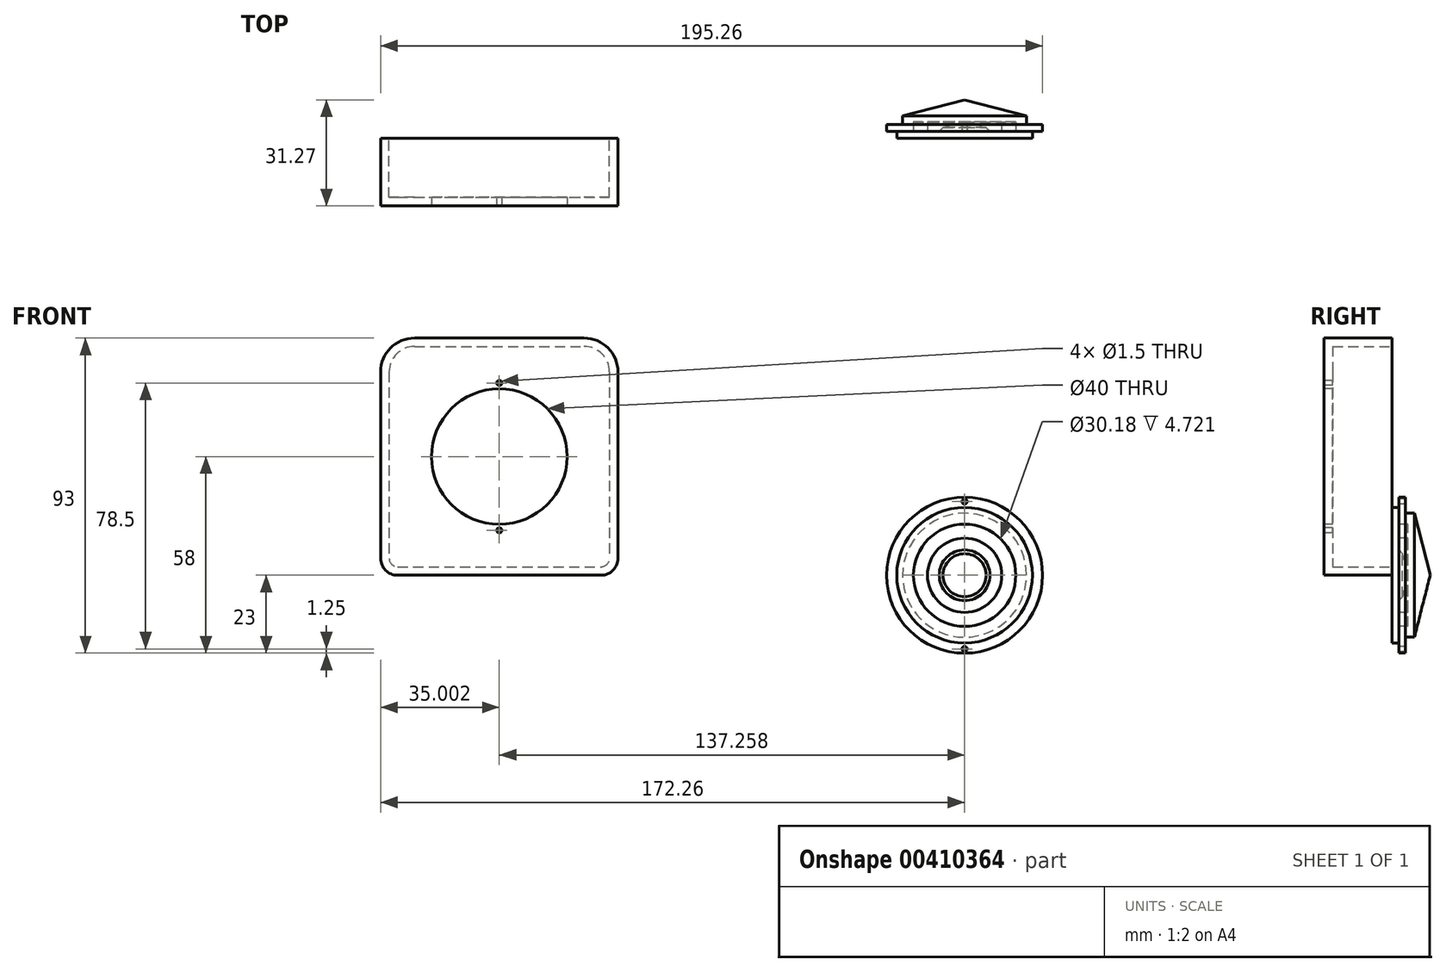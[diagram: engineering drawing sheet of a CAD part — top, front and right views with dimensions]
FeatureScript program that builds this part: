
annotation { "Feature Type Name" : "Feature", "Feature Type Description" : "" }
export const myFeature = defineFeature(function(context is Context, id is Id, definition is map)
    precondition{}
    {
        {
            var Q0;
            Q0=qCreatedBy(makeId("Right.planeOp"),FACE);
            var sketch = newSketch(context, id + "F0", { "sketchPlane" : qUnion([Q0])});
            skLineSegment(sketch, "E0", {"start": v(0, 20) * mm, "end": v(2, 20) * mm});
            skLineSegment(sketch, "E1", {"start": v(0, 20) * mm, "end": v(0, 15.09) * mm});
            skLineSegment(sketch, "E2", {"start": v(0, 15.09) * mm, "end": v(2, 15.09) * mm});
            skLineSegment(sketch, "E3", {"start": v(2, 11.08) * mm, "end": v(2.03, 10.95) * mm});
            skPoint(sketch, "E3.endSnap0", {"position": v(2.86, 0) * mm});
            skLineSegment(sketch, "E4", {"start": v(4.58, 0) * mm, "end": v(6.88, 0) * mm});
            skLineSegment(sketch, "E5", {"start": v(2, 20) * mm, "end": v(2, 23) * mm});
            skLineSegment(sketch, "E6", {"start": v(2, 23) * mm, "end": v(4, 23) * mm});
            skLineSegment(sketch, "E7", {"start": v(4, 23) * mm, "end": v(4, 19.74) * mm});
            skLineSegment(sketch, "E8", {"start": v(4, 19.74) * mm, "end": v(4, 18.29) * mm});
            skLineSegment(sketch, "E9", {"start": v(4, 18.29) * mm, "end": v(6.62, 18.29) * mm});
            skLineSegment(sketch, "E10", {"start": v(11.27, 0) * mm, "end": v(6.88, 0) * mm});
            skLineSegment(sketch, "E11", {"start": v(6.62, 18.29) * mm, "end": v(11.27, 0) * mm});
            skLineSegment(sketch, "E12", {"start": v(2, 15.09) * mm, "end": v(4.72, 15.09) * mm});
            skLineSegment(sketch, "E13", {"start": v(4.72, 15.09) * mm, "end": v(4.72, 10.95) * mm});
            skLineSegment(sketch, "E14", {"start": v(4.72, 10.95) * mm, "end": v(2.03, 10.95) * mm});
            skLineSegment(sketch, "E15", {"start": v(2.03, 10.95) * mm, "end": v(2.03, 7.48) * mm});
            skLineSegment(sketch, "E16", {"start": v(2.03, 7.48) * mm, "end": v(3.1, 6.34) * mm});
            skLineSegment(sketch, "E17.trimOffspring", {"start": v(3.1, 6.34) * mm, "end": v(4.58, 0) * mm});
            skSolve(sketch);
        }
        {
            var Q0;
            Q0 = qSketchRegion(id + "F0", true);
            var Q1;
            Q1=sQuery(id+"F0.wireOp",EDGE,"E4");
            revolve(context, id + "F1", {"entities" : qUnion([Q0]), "axis" : qUnion([Q1]), "revolveType" : RevolveType.FULL});
        }
        {
            var Q0;
            Q0=makeQuery(id+"F1.opRevolve","SWEPT_FACE",FACE,{"disambiguationData":[OSD([sQuery(id+"F0.wireOp",EDGE,"E5")])]});
            var sketch = newSketch(context, id + "F2", { "sketchPlane" : qUnion([Q0])});
            skCircle(sketch, "E18", {"center": v(0, 21.75) * mm, "radius": 0.75 * mm});
            skCircle(sketch, "E19.MirrorC", {"center": v(0, -21.75) * mm, "radius": 0.75 * mm});
            skSolve(sketch);
        }
        {
            var Q0;
            Q0 = qSketchRegion(id + "F2", true);
            extrude(context, id + "F3", {"entities" : qUnion([Q0]), "operationType" : NewBodyOperationType.REMOVE, "oppositeDirection" : true, "depth" : 25 * mm});
        }
        {
            var Q0;
            Q0=qCreatedBy(makeId("Front.planeOp"),FACE);
            var sketch = newSketch(context, id + "F4", { "sketchPlane" : qUnion([Q0])});
            skLineSegment(sketch, "E20.bottom", {"start": v(-162.26, 70) * mm, "end": v(-112.26, 70) * mm});
            skLineSegment(sketch, "E20.top", {"start": v(-167.26, 0) * mm, "end": v(-107.26, 0) * mm});
            skLineSegment(sketch, "E20.left", {"start": v(-172.26, 60) * mm, "end": v(-172.26, 5) * mm});
            skLineSegment(sketch, "E20.right", {"start": v(-102.26, 60) * mm, "end": v(-102.26, 5) * mm});
            skPoint(sketch, "E21.visualSharp", {"position": v(-172.26, 70) * mm});
            skArc(sketch, "E21.filletArc", {"start": v(-162.26, 70) * mm, "mid": v(-169.33, 67.07) * mm, "end": v(-172.26, 60) * mm});
            skPoint(sketch, "E22.visualSharp", {"position": v(-102.26, 70) * mm});
            skArc(sketch, "E22.filletArc", {"start": v(-102.26, 60) * mm, "mid": v(-105.19, 67.07) * mm, "end": v(-112.26, 70) * mm});
            skPoint(sketch, "E23.visualSharp", {"position": v(-172.26, 0) * mm});
            skArc(sketch, "E23.filletArc", {"start": v(-172.26, 5) * mm, "mid": v(-170.8, 1.46) * mm, "end": v(-167.26, 0) * mm});
            skPoint(sketch, "E24.visualSharp", {"position": v(-102.26, 0) * mm});
            skArc(sketch, "E24.filletArc", {"start": v(-107.26, 0) * mm, "mid": v(-103.72, 1.46) * mm, "end": v(-102.26, 5) * mm});
            skSolve(sketch);
        }
        {
            var Q0;
            Q0=makeQuery(id+"F4.imprint","IMPRINT",FACE,{"disambiguationData":[TD([[makeQuery(id+"F4.imprint","IMPRINT",EDGE,{"derivedFrom":sQuery(id+"F4.wireOp",EDGE,"E20.bottom")}),-1.0]])]});
            extrude(context, id + "F5", {"entities" : qUnion([Q0]), "depth" : 20 * mm});
        }
        {
            var Q0;
            Q0=makeQuery(id+"F5.opExtrude","CAP_FACE",FACE,{"disambiguationData":[OSD([sQuery(id+"F4.wireOp",EDGE,"E20.bottom"),sQuery(id+"F4.wireOp",EDGE,"E20.top"),sQuery(id+"F4.wireOp",EDGE,"E20.left"),sQuery(id+"F4.wireOp",EDGE,"E20.right")])],"isStart":true});
            shell(context, id + "F6", {"entities" : qUnion([Q0]), "thickness" : 2.5 * mm});
        }
        {
            var Q0;
            Q0=makeQuery(id+"F5.opExtrude","CAP_FACE",FACE,{"disambiguationData":[OSD([sQuery(id+"F4.wireOp",EDGE,"E20.bottom"),sQuery(id+"F4.wireOp",EDGE,"E20.top"),sQuery(id+"F4.wireOp",EDGE,"E20.left"),sQuery(id+"F4.wireOp",EDGE,"E20.right")])],"isStart":false});
            var sketch = newSketch(context, id + "F7", { "sketchPlane" : qUnion([Q0])});
            skCircle(sketch, "E25", {"center": v(-137.26, 35) * mm, "radius": 20 * mm});
            skSolve(sketch);
        }
        {
            var Q0;
            Q0=makeQuery(id+"F7.imprint","IMPRINT",FACE,{"disambiguationData":[TD([[makeQuery(id+"F7.imprint","IMPRINT",EDGE,{"derivedFrom":sQuery(id+"F7.wireOp",EDGE,"E25")}),1.0]])]});
            extrude(context, id + "F8", {"entities" : qUnion([Q0]), "operationType" : NewBodyOperationType.REMOVE, "oppositeDirection" : true, "depth" : 25 * mm});
        }
        {
            var Q0;
            Q0=makeQuery(id+"F5.opExtrude","CAP_FACE",FACE,{"disambiguationData":[OSD([sQuery(id+"F4.wireOp",EDGE,"E20.bottom"),sQuery(id+"F4.wireOp",EDGE,"E20.top"),sQuery(id+"F4.wireOp",EDGE,"E20.left"),sQuery(id+"F4.wireOp",EDGE,"E20.right")])],"isStart":false});
            var sketch = newSketch(context, id + "F9", { "sketchPlane" : qUnion([Q0])});
            skCircle(sketch, "E26", {"center": v(-137.26, 56.75) * mm, "radius": 0.75 * mm});
            skLineSegment(sketch, "E27", {"start": v(-188.1, 35) * mm, "end": v(-94.85, 35) * mm});
            skCircle(sketch, "E28.MirrorC", {"center": v(-137.26, 13.25) * mm, "radius": 0.75 * mm});
            skSolve(sketch);
        }
        {
            var Q0;
            Q0 = qSketchRegion(id + "F9", true);
            extrude(context, id + "F10", {"entities" : qUnion([Q0]), "operationType" : NewBodyOperationType.REMOVE, "oppositeDirection" : true, "depth" : 25 * mm});
        }
    });
